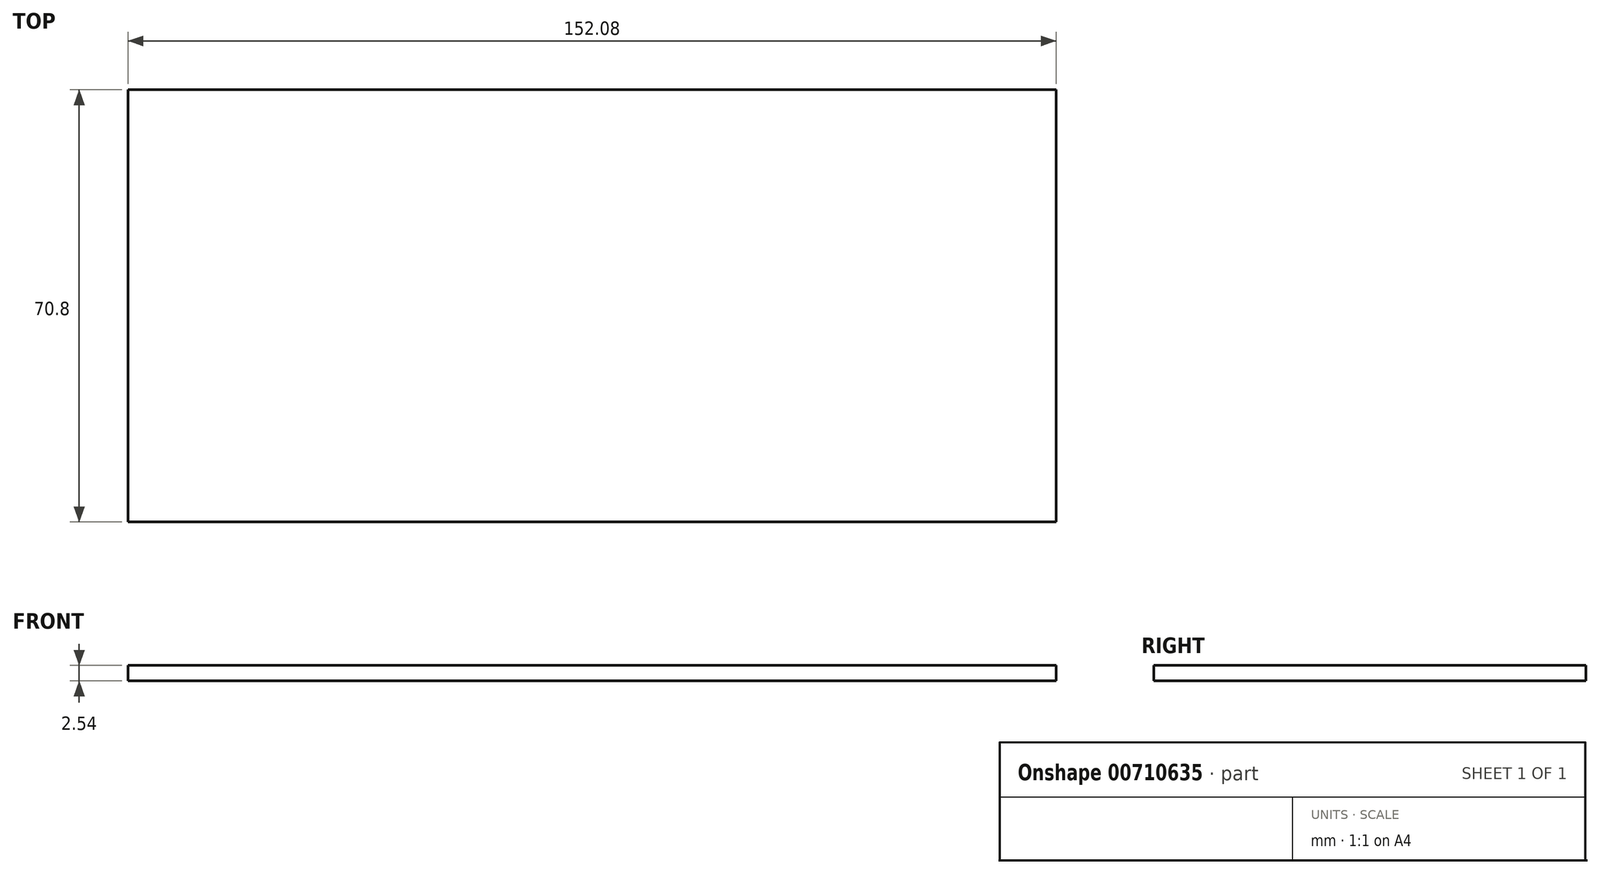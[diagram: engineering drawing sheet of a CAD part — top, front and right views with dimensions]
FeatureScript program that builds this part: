
annotation { "Feature Type Name" : "Feature", "Feature Type Description" : "" }
export const myFeature = defineFeature(function(context is Context, id is Id, definition is map)
    precondition{}
    {
        {
            var Q0;
            Q0=qCreatedBy(makeId("Top.planeOp"),FACE);
            var sketch = newSketch(context, id + "F0", { "sketchPlane" : qUnion([Q0])});
            skLineSegment(sketch, "E0.bottom", {"start": v(-76.04, 35.4) * mm, "end": v(76.04, 35.4) * mm});
            skLineSegment(sketch, "E0.top", {"start": v(-76.04, -35.4) * mm, "end": v(76.04, -35.4) * mm});
            skLineSegment(sketch, "E0.left", {"start": v(-76.04, 35.4) * mm, "end": v(-76.04, -35.4) * mm});
            skLineSegment(sketch, "E0.right", {"start": v(76.04, 35.4) * mm, "end": v(76.04, -35.4) * mm});
            skPoint(sketch, "E0.middle", {"position": v(0, 0) * mm});
            skSolve(sketch);
        }
        {
            var Q0;
            Q0=makeQuery(id+"F0.imprint","IMPRINT",FACE,{"disambiguationData":[TD([[makeQuery(id+"F0.imprint","IMPRINT",EDGE,{"derivedFrom":sQuery(id+"F0.wireOp",EDGE,"E0.bottom")}),-1.0]])]});
            extrude(context, id + "F1", {"entities" : qUnion([Q0]), "depth" : 2.54 * mm, "offsetDistance" : 25.4 * mm});
        }
    });
